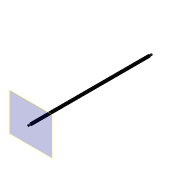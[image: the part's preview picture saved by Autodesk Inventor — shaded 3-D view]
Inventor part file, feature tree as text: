
AUTODESK INVENTOR PART (.ipt)
format: ipt  version: 2014 (Build 180170000, 170)  size: 98,304 bytes
history: native  units: mm
features: extrude x5, sketch x5, thread x2, chamfer x2, plane x1
ambient origin geometry x8: Origin, YZ Plane, XZ Plane, XY Plane, X Axis, Y Axis, Z Axis, Center Point
bodies: Body1 (feature_tree)
feature tree (15):
  plane  "Work Plane1"
  extrude  "Extrusion1"  Depth=6.0mm
  extrude  "Extrusion2"  Depth=3.0mm
  extrude  "Extrusion3"  Depth=10.0mm
  thread  "Thread1"  [1 undecoded]
  chamfer  "Chamfer2"  Distance=10.0mm
  extrude  "Extrusion4"  Depth=3.0mm
  extrude  "Extrusion5"  Depth=2.0mm
  thread  "Thread2"  [1 undecoded]
  chamfer  "Chamfer3"  Distance=10.0mm
  sketch  "Sketch2"  dims[d4=3.0mm d6=6.0mm]
  sketch  "Sketch5"  dims[d7=251.0mm d8=0.0mm d26=3.0mm]
  sketch  "Sketch6"  dims[d27=6.0mm d28=0.0mm d29=4.0mm d30=5.0mm d31=0.0mm d32=10.0mm d33=0.0mm]
  sketch  "Sketch7"  dims[d34=0.3mm d35=2.0mm d36=45.0deg d37=3.0mm]
  sketch  "Sketch8"  dims[d38=6.0mm d39=0.0mm d40=4.0mm d41=5.0mm d42=0.0mm d43=10.0mm d44=0.0mm d45=0.3mm d46=2.0mm d47=45.0deg]
note: 2 required parameter values undecoded (feature->parameter linkage not recoverable at this tier; creation-order binding heuristic only, values carry confidence <= 0.55)
